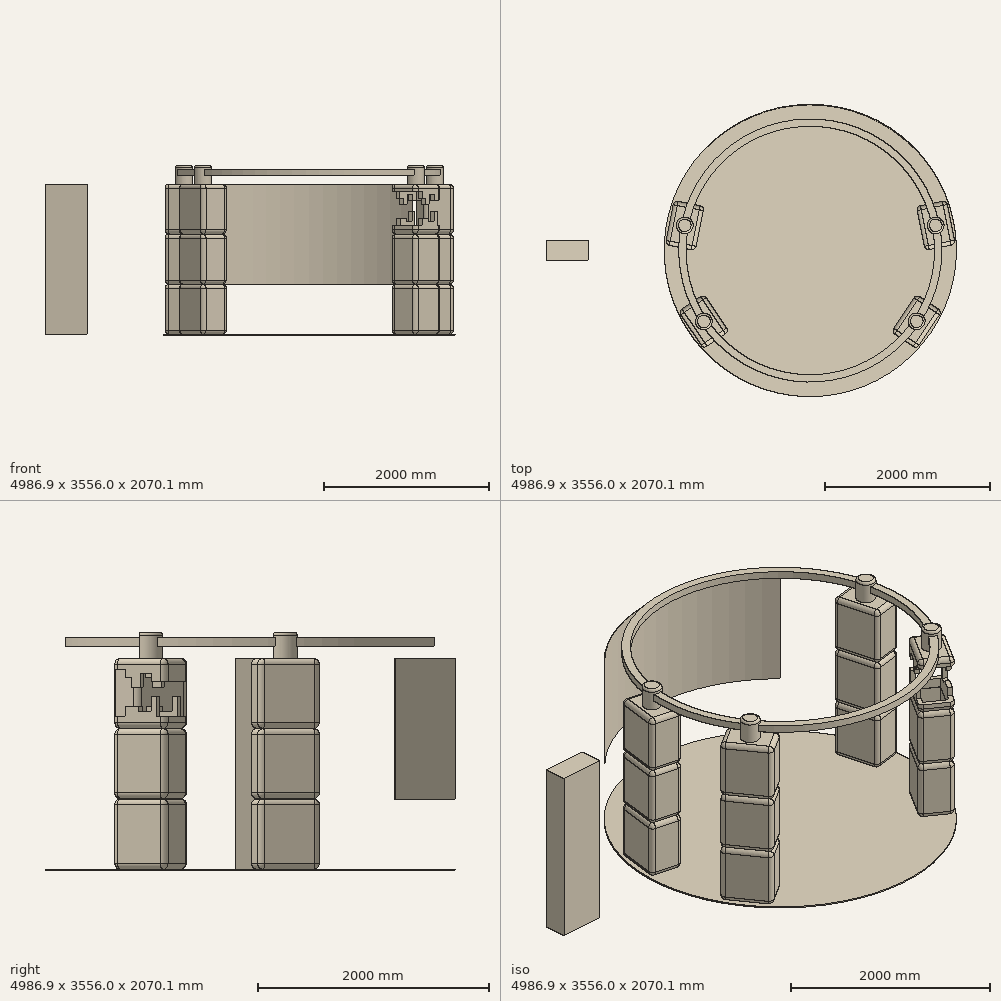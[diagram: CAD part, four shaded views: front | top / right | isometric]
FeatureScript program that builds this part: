
annotation { "Feature Type Name" : "Feature", "Feature Type Description" : "" }
export const myFeature = defineFeature(function(context is Context, id is Id, definition is map)
    precondition{}
    {
        {
            var Q0;
            Q0=qCreatedBy(makeId("Top.planeOp"),FACE);
            var sketch = newSketch(context, id + "F0", { "sketchPlane" : qUnion([Q0])});
            skCircle(sketch, "E0", {"center": v(0, 0) * mm, "radius": 1778 * mm});
            skSolve(sketch);
        }
        {
            var Q0;
            Q0 = qSketchRegion(id + "F0", true);
            extrude(context, id + "F1", {"entities" : qUnion([Q0]), "oppositeDirection" : true, "depth" : 12.7 * mm, "offsetDistance" : 25.4 * mm});
        }
        {
            var Q0;
            Q0=makeQuery(id+"F1.opExtrude","CAP_FACE",FACE,{"disambiguationData":[OSD([sQuery(id+"F0.wireOp",EDGE,"E0")])],"isStart":true});
            var sketch = newSketch(context, id + "F2", { "sketchPlane" : qUnion([Q0])});
            skLineSegment(sketch, "E1", {"start": v(0, -1778) * mm, "end": v(0, 1778) * mm});
            skLineSegment(sketch, "E2", {"start": v(-1778, 0) * mm, "end": v(1778, 0) * mm});
            skLineSegment(sketch, "E3.bottom", {"start": v(-1778, -1778) * mm, "end": v(1778, -1778) * mm});
            skLineSegment(sketch, "E3.top", {"start": v(-1778, 1778) * mm, "end": v(1778, 1778) * mm});
            skLineSegment(sketch, "E3.left", {"start": v(-1778, -1778) * mm, "end": v(-1778, 1778) * mm});
            skLineSegment(sketch, "E3.right", {"start": v(1778, -1778) * mm, "end": v(1778, 1778) * mm});
            skPoint(sketch, "E3.middle", {"position": v(0, 0) * mm});
            skLineSegment(sketch, "E4", {"start": v(-1778, -1778) * mm, "end": v(1778, 1778) * mm});
            skLineSegment(sketch, "E5", {"start": v(1778, -1778) * mm, "end": v(-1778, 1778) * mm});
            skCircle(sketch, "E6", {"center": v(0, 0) * mm, "radius": 1778 * mm});
            skCircle(sketch, "E7", {"center": v(0, 0) * mm, "radius": 1905 * mm});
            skLineSegment(sketch, "E8", {"start": v(0, -1422.31) * mm, "end": v(-1066.92, -1422.31) * mm});
            skLineSegment(sketch, "E9", {"start": v(0, -1422.31) * mm, "end": v(1066.92, -1422.31) * mm});
            skLineSegment(sketch, "E10", {"start": v(0, 0) * mm, "end": v(-1066.92, -1422.31) * mm});
            skLineSegment(sketch, "E11", {"start": v(0, 0) * mm, "end": v(1066.92, -1422.31) * mm});
            skLineSegment(sketch, "E12", {"start": v(0, 0) * mm, "end": v(-1143.12, -1523.9) * mm});
            skLineSegment(sketch, "E13", {"start": v(0, 0) * mm, "end": v(1143.12, -1523.9) * mm});
            skSolve(sketch);
        }
        {
            var Q0;
            Q0=makeQuery(id+"F1.opExtrude","CAP_FACE",FACE,{"disambiguationData":[OSD([sQuery(id+"F0.wireOp",EDGE,"E0")])],"isStart":true});
            var sketch = newSketch(context, id + "F3", { "sketchPlane" : qUnion([Q0])});
            skLineSegment(sketch, "E14.bottom", {"start": v(-1778, 1778) * mm, "end": v(1778, 1778) * mm});
            skLineSegment(sketch, "E14.top", {"start": v(-1778, -1778) * mm, "end": v(1778, -1778) * mm});
            skLineSegment(sketch, "E14.left", {"start": v(-1778, 1778) * mm, "end": v(-1778, -1778) * mm});
            skLineSegment(sketch, "E14.right", {"start": v(1778, 1778) * mm, "end": v(1778, -1778) * mm});
            skPoint(sketch, "E14.middle", {"position": v(0, 0) * mm});
            skLineSegment(sketch, "E15", {"start": v(1778, 1778) * mm, "end": v(-1778, -1778) * mm});
            skLineSegment(sketch, "E16", {"start": v(-1778, 1778) * mm, "end": v(1778, -1778) * mm});
            skLineSegment(sketch, "E17", {"start": v(1778, 0) * mm, "end": v(-1778, 0) * mm});
            skLineSegment(sketch, "E18", {"start": v(-1778, -1778) * mm, "end": v(-1778, -889) * mm});
            skLineSegment(sketch, "E19", {"start": v(-1778, -889) * mm, "end": v(1778, -889) * mm});
            skLineSegment(sketch, "E20", {"start": v(-1778, 1778) * mm, "end": v(-1778, 889) * mm});
            skLineSegment(sketch, "E21", {"start": v(-1517.62, -628.62) * mm, "end": v(1517.62, 628.62) * mm});
            skLineSegment(sketch, "E22", {"start": v(1517.62, -628.62) * mm, "end": v(-1517.62, 628.62) * mm});
            skLineSegment(sketch, "E23", {"start": v(1404.74, 581.86) * mm, "end": v(1642.66, 680.41) * mm});
            skLineSegment(sketch, "E24", {"start": v(-1394.59, -577.66) * mm, "end": v(-1642.66, -680.41) * mm});
            skLineSegment(sketch, "E25", {"start": v(-1411, 584.46) * mm, "end": v(-1642.66, 680.41) * mm});
            skLineSegment(sketch, "E26", {"start": v(1385, -573.69) * mm, "end": v(1642.66, -680.41) * mm});
            skLineSegment(sketch, "E27", {"start": v(-1290.66, 534.6) * mm, "end": v(-1397, 0) * mm});
            skLineSegment(sketch, "E28", {"start": v(-1642.66, 680.41) * mm, "end": v(-1778, 0) * mm});
            skLineSegment(sketch, "E29", {"start": v(-1290.66, 534.6) * mm, "end": v(-1657.16, 607.5) * mm});
            skLineSegment(sketch, "E30", {"start": v(-1397, 0) * mm, "end": v(-1763.5, 72.9) * mm});
            skLineSegment(sketch, "E31", {"start": v(-1290.66, -534.6) * mm, "end": v(-987.83, -987.83) * mm});
            skLineSegment(sketch, "E32", {"start": v(-1257.24, -1257.24) * mm, "end": v(-1642.66, -680.41) * mm});
            skLineSegment(sketch, "E33", {"start": v(-1290.66, -534.6) * mm, "end": v(-1601.36, -742.21) * mm});
            skLineSegment(sketch, "E34", {"start": v(-987.83, -987.83) * mm, "end": v(-1298.53, -1195.43) * mm});
            skLineSegment(sketch, "E35", {"start": v(1290.66, -534.6) * mm, "end": v(987.83, -987.83) * mm});
            skLineSegment(sketch, "E36", {"start": v(1642.66, -680.41) * mm, "end": v(1257.24, -1257.24) * mm});
            skLineSegment(sketch, "E37", {"start": v(987.83, -987.83) * mm, "end": v(1298.53, -1195.43) * mm});
            skLineSegment(sketch, "E38", {"start": v(1290.66, -534.6) * mm, "end": v(1601.36, -742.21) * mm});
            skLineSegment(sketch, "E39", {"start": v(1642.66, 680.41) * mm, "end": v(1778, 0) * mm});
            skLineSegment(sketch, "E40", {"start": v(1290.66, 534.6) * mm, "end": v(1397, 0) * mm});
            skLineSegment(sketch, "E41", {"start": v(1397, 0) * mm, "end": v(1763.5, 72.9) * mm});
            skLineSegment(sketch, "E42", {"start": v(1290.66, 534.6) * mm, "end": v(1657.16, 607.5) * mm});
            skSolve(sketch);
        }
        {
            var Q0;
            Q0=qCreatedBy(makeId("Top.planeOp"),FACE);
            var sketch = newSketch(context, id + "F4", { "sketchPlane" : qUnion([Q0])});
            skLineSegment(sketch, "E43.bottom", {"start": v(-2700.9, -127) * mm, "end": v(-3208.9, -127) * mm});
            skLineSegment(sketch, "E43.top", {"start": v(-2700.9, 127) * mm, "end": v(-3208.9, 127) * mm});
            skLineSegment(sketch, "E43.left", {"start": v(-2700.9, -127) * mm, "end": v(-2700.9, 127) * mm});
            skLineSegment(sketch, "E43.right", {"start": v(-3208.9, -127) * mm, "end": v(-3208.9, 127) * mm});
            skPoint(sketch, "E43.middle", {"position": v(-2954.9, 0) * mm});
            skSolve(sketch);
        }
        {
            var Q0;
            Q0=makeQuery(id+"F4.imprint","IMPRINT",FACE,{"disambiguationData":[TD([[makeQuery(id+"F4.imprint","IMPRINT",EDGE,{"derivedFrom":sQuery(id+"F4.wireOp",EDGE,"E43.bottom")}),-1.0]])]});
            extrude(context, id + "F5", {"entities" : qUnion([Q0]), "depth" : 1828.8 * mm, "offsetDistance" : 25.4 * mm});
        }
        {
            var Q0;
            Q0=makeQuery(id+"F3.imprint","IMPRINT",FACE,{"disambiguationData":[TD([[makeQuery(id+"F3.imprint","IMPRINT",EDGE,{"derivedFrom":sQuery(id+"F3.wireOp",EDGE,"E27")}),-1.0]])]});
            var Q1;
            Q1=makeQuery(id+"F3.imprint","IMPRINT",FACE,{"disambiguationData":[TD([[makeQuery(id+"F3.imprint","IMPRINT",EDGE,{"derivedFrom":sQuery(id+"F3.wireOp",EDGE,"E40")}),1.0]])]});
            var Q2;
            {var subQ5=sQuery(id+"F3.wireOp",EDGE,"E33");Q2=makeQuery(id+"F3.imprint","IMPRINT",FACE,{"disambiguationData":[TD([[makeQuery(id+"F3.imprint","IMPRINT",EDGE,{"derivedFrom":subQ5}),1.0]])]});}
            var Q3;
            {var subQ5=sQuery(id+"F3.wireOp",EDGE,"E34");Q3=makeQuery(id+"F3.imprint","IMPRINT",FACE,{"disambiguationData":[TD([[makeQuery(id+"F3.imprint","IMPRINT",EDGE,{"derivedFrom":subQ5}),-1.0]])]});}
            var Q4;
            {var subQ5=sQuery(id+"F3.wireOp",EDGE,"E38");Q4=makeQuery(id+"F3.imprint","IMPRINT",FACE,{"disambiguationData":[TD([[makeQuery(id+"F3.imprint","IMPRINT",EDGE,{"derivedFrom":subQ5}),-1.0]])]});}
            var Q5;
            {var subQ5=sQuery(id+"F3.wireOp",EDGE,"E37");Q5=makeQuery(id+"F3.imprint","IMPRINT",FACE,{"disambiguationData":[TD([[makeQuery(id+"F3.imprint","IMPRINT",EDGE,{"derivedFrom":subQ5}),1.0]])]});}
            extrude(context, id + "F6", {"entities" : qUnion([Q0, Q1, Q2, Q3, Q4, Q5]), "depth" : 1828.8 * mm, "offsetDistance" : 25.4 * mm});
        }
        {
            var Q0;
            Q0=qCreatedBy(makeId("Front.planeOp"),FACE);
            var sketch = newSketch(context, id + "F7", { "sketchPlane" : qUnion([Q0])});
            skLineSegment(sketch, "E44", {"start": v(-207.03, 0) * mm, "end": v(-207.03, 609.6) * mm});
            skLineSegment(sketch, "E45", {"start": v(-207.03, 609.6) * mm, "end": v(-207.03, 1219.2) * mm});
            skLineSegment(sketch, "E46", {"start": v(-207.03, 1219.2) * mm, "end": v(-207.03, 1828.8) * mm});
            skLineSegment(sketch, "E47.bottom", {"start": v(-1849.74, 609.6) * mm, "end": v(1833.26, 609.6) * mm});
            skLineSegment(sketch, "E47.top", {"start": v(-1849.74, 612.14) * mm, "end": v(1833.26, 612.14) * mm});
            skLineSegment(sketch, "E47.left", {"start": v(-1849.74, 609.6) * mm, "end": v(-1849.74, 612.14) * mm});
            skLineSegment(sketch, "E47.right", {"start": v(1833.26, 609.6) * mm, "end": v(1833.26, 612.14) * mm});
            skLineSegment(sketch, "E48.bottom", {"start": v(-1849.74, 1219.2) * mm, "end": v(1833.26, 1219.2) * mm});
            skLineSegment(sketch, "E48.top", {"start": v(-1849.74, 1221.74) * mm, "end": v(1833.26, 1221.74) * mm});
            skLineSegment(sketch, "E48.left", {"start": v(-1849.74, 1219.2) * mm, "end": v(-1849.74, 1221.74) * mm});
            skLineSegment(sketch, "E48.right", {"start": v(1833.26, 1219.2) * mm, "end": v(1833.26, 1221.74) * mm});
            skSolve(sketch);
        }
        {
            var Q0;
            Q0 = qSketchRegion(id + "F7", true);
            extrude(context, id + "F8", {"entities" : qUnion([Q0]), "operationType" : NewBodyOperationType.REMOVE, "oppositeDirection" : true, "depth" : 1447.8 * mm, "offsetDistance" : 25.4 * mm, "hasSecondDirection" : true, "secondDirectionOppositeDirection" : false, "secondDirectionDepth" : 1905 * mm});
        }
        {
            var Q0;
            Q0=makeQuery(id+"F6.opExtrude","CAP_FACE",FACE,{"disambiguationData":[OSD([sQuery(id+"F3.wireOp",EDGE,"E39"),sQuery(id+"F3.wireOp",EDGE,"E40"),sQuery(id+"F3.wireOp",EDGE,"E41"),sQuery(id+"F3.wireOp",EDGE,"E42")])],"isStart":false});
            var Q1;
            {var subQ1=sQuery(id+"F3.wireOp",EDGE,"E42");Q1=makeQuery(id+"F8.boolean.opBoolean","SPLIT",FACE,{"disambiguationData":[TD([makeQuery(id+"F8.opExtrude","SWEPT_FACE",FACE,{"disambiguationData":[OSD([sQuery(id+"F7.wireOp",EDGE,"E48.top")])]})])],"derivedFrom":makeQuery(id+"F6.opExtrude","SWEPT_FACE",FACE,{"disambiguationData":[OSD([subQ1])]})});}
            var Q2;
            {var subQ2=sQuery(id+"F3.wireOp",EDGE,"E40");Q2=makeQuery(id+"F8.boolean.opBoolean","SPLIT",FACE,{"disambiguationData":[TD([makeQuery(id+"F8.opExtrude","SWEPT_FACE",FACE,{"disambiguationData":[OSD([sQuery(id+"F7.wireOp",EDGE,"E48.top")])]})])],"derivedFrom":makeQuery(id+"F6.opExtrude","SWEPT_FACE",FACE,{"disambiguationData":[OSD([subQ2])]})});}
            var Q3;
            {var subQ1=sQuery(id+"F3.wireOp",EDGE,"E41");Q3=makeQuery(id+"F8.boolean.opBoolean","SPLIT",FACE,{"disambiguationData":[TD([makeQuery(id+"F8.opExtrude","SWEPT_FACE",FACE,{"disambiguationData":[OSD([sQuery(id+"F7.wireOp",EDGE,"E48.top")])]})])],"derivedFrom":makeQuery(id+"F6.opExtrude","SWEPT_FACE",FACE,{"disambiguationData":[OSD([subQ1])]})});}
            var Q4;
            {var subQ2=sQuery(id+"F3.wireOp",EDGE,"E39");Q4=makeQuery(id+"F8.boolean.opBoolean","SPLIT",FACE,{"disambiguationData":[TD([makeQuery(id+"F8.opExtrude","SWEPT_FACE",FACE,{"disambiguationData":[OSD([sQuery(id+"F7.wireOp",EDGE,"E48.top")])]})])],"derivedFrom":makeQuery(id+"F6.opExtrude","SWEPT_FACE",FACE,{"disambiguationData":[OSD([subQ2])]})});}
            var Q5;
            Q5=makeQuery(id+"F8.boolean.opBoolean","SPLIT",FACE,{"disambiguationData":[TD([makeQuery(id+"F8.opExtrude","SWEPT_FACE",FACE,{"disambiguationData":[OSD([sQuery(id+"F7.wireOp",EDGE,"E47.top")])]})])],"derivedFrom":makeQuery(id+"F6.opExtrude","SWEPT_FACE",FACE,{"disambiguationData":[OSD([sQuery(id+"F3.wireOp",EDGE,"E39")])]})});
            var Q6;
            Q6=makeQuery(id+"F8.boolean.opBoolean","SPLIT",FACE,{"disambiguationData":[TD([makeQuery(id+"F8.opExtrude","SWEPT_FACE",FACE,{"disambiguationData":[OSD([sQuery(id+"F7.wireOp",EDGE,"E47.top")])]})])],"derivedFrom":makeQuery(id+"F6.opExtrude","SWEPT_FACE",FACE,{"disambiguationData":[OSD([sQuery(id+"F3.wireOp",EDGE,"E40")])]})});
            var Q7;
            Q7=makeQuery(id+"F8.boolean.opBoolean","SPLIT",FACE,{"disambiguationData":[TD([makeQuery(id+"F8.opExtrude","SWEPT_FACE",FACE,{"disambiguationData":[OSD([sQuery(id+"F7.wireOp",EDGE,"E47.top")])]})])],"derivedFrom":makeQuery(id+"F6.opExtrude","SWEPT_FACE",FACE,{"disambiguationData":[OSD([sQuery(id+"F3.wireOp",EDGE,"E41")])]})});
            var Q8;
            Q8=makeQuery(id+"F8.boolean.opBoolean","SPLIT",FACE,{"disambiguationData":[TD([makeQuery(id+"F8.opExtrude","SWEPT_FACE",FACE,{"disambiguationData":[OSD([sQuery(id+"F7.wireOp",EDGE,"E47.top")])]})])],"derivedFrom":makeQuery(id+"F6.opExtrude","SWEPT_FACE",FACE,{"disambiguationData":[OSD([sQuery(id+"F3.wireOp",EDGE,"E42")])]})});
            var Q9;
            Q9=makeQuery(id+"F8.boolean.opBoolean","SPLIT",FACE,{"disambiguationData":[TD([makeQuery(id+"F8.opExtrude","SWEPT_FACE",FACE,{"disambiguationData":[OSD([sQuery(id+"F7.wireOp",EDGE,"E47.top")])]})])],"derivedFrom":makeQuery(id+"F6.opExtrude","SWEPT_FACE",FACE,{"disambiguationData":[OSD([sQuery(id+"F3.wireOp",EDGE,"E36")])]})});
            var Q10;
            {var subQ2=sQuery(id+"F3.wireOp",EDGE,"E36");Q10=makeQuery(id+"F8.boolean.opBoolean","SPLIT",FACE,{"disambiguationData":[TD([makeQuery(id+"F8.opExtrude","SWEPT_FACE",FACE,{"disambiguationData":[OSD([sQuery(id+"F7.wireOp",EDGE,"E48.top")])]})])],"derivedFrom":makeQuery(id+"F6.opExtrude","SWEPT_FACE",FACE,{"disambiguationData":[OSD([subQ2])]})});}
            var Q11;
            Q11=makeQuery(id+"F6.opExtrude","CAP_FACE",FACE,{"disambiguationData":[OSD([sQuery(id+"F3.wireOp",EDGE,"E35"),sQuery(id+"F3.wireOp",EDGE,"E36"),sQuery(id+"F3.wireOp",EDGE,"E37"),sQuery(id+"F3.wireOp",EDGE,"E38")])],"isStart":false});
            var Q12;
            {var subQ1=sQuery(id+"F3.wireOp",EDGE,"E38");Q12=makeQuery(id+"F8.boolean.opBoolean","SPLIT",FACE,{"disambiguationData":[TD([makeQuery(id+"F8.opExtrude","SWEPT_FACE",FACE,{"disambiguationData":[OSD([sQuery(id+"F7.wireOp",EDGE,"E48.top")])]})])],"derivedFrom":makeQuery(id+"F6.opExtrude","SWEPT_FACE",FACE,{"disambiguationData":[OSD([subQ1])]})});}
            var Q13;
            {var subQ0=sQuery(id+"F3.wireOp",EDGE,"E35");var subQ1=sQuery(id+"F3.wireOp",EDGE,"E38");Q13=makeQuery(id+"F8.boolean.opBoolean","SPLIT",EDGE,{"disambiguationData":[TD([makeQuery(id+"F8.opExtrude","SWEPT_FACE",FACE,{"disambiguationData":[OSD([sQuery(id+"F7.wireOp",EDGE,"E47.top")])]})])],"derivedFrom":makeQuery(id+"F6.opExtrude","SWEPT_EDGE",EDGE,{"disambiguationData":[OSD([sQuery(id+"F3.wireOp",EDGE,"E22"),subQ0,subQ1])]})});}
            var Q14;
            {var subQ2=sQuery(id+"F3.wireOp",EDGE,"E35");Q14=makeQuery(id+"F8.boolean.opBoolean","SPLIT",FACE,{"disambiguationData":[TD([makeQuery(id+"F8.opExtrude","SWEPT_FACE",FACE,{"disambiguationData":[OSD([sQuery(id+"F7.wireOp",EDGE,"E48.top")])]})])],"derivedFrom":makeQuery(id+"F6.opExtrude","SWEPT_FACE",FACE,{"disambiguationData":[OSD([subQ2])]})});}
            var Q15;
            Q15=makeQuery(id+"F8.boolean.opBoolean","SPLIT",FACE,{"disambiguationData":[TD([makeQuery(id+"F8.opExtrude","SWEPT_FACE",FACE,{"disambiguationData":[OSD([sQuery(id+"F7.wireOp",EDGE,"E47.top")])]})])],"derivedFrom":makeQuery(id+"F6.opExtrude","SWEPT_FACE",FACE,{"disambiguationData":[OSD([sQuery(id+"F3.wireOp",EDGE,"E35")])]})});
            var Q16;
            Q16=makeQuery(id+"F6.opExtrude","CAP_FACE",FACE,{"disambiguationData":[OSD([sQuery(id+"F3.wireOp",EDGE,"E27"),sQuery(id+"F3.wireOp",EDGE,"E28"),sQuery(id+"F3.wireOp",EDGE,"E29"),sQuery(id+"F3.wireOp",EDGE,"E30")])],"isStart":false});
            var Q17;
            {var subQ1=sQuery(id+"F3.wireOp",EDGE,"E29");Q17=makeQuery(id+"F8.boolean.opBoolean","SPLIT",FACE,{"disambiguationData":[TD([makeQuery(id+"F8.opExtrude","SWEPT_FACE",FACE,{"disambiguationData":[OSD([sQuery(id+"F7.wireOp",EDGE,"E48.top")])]})])],"derivedFrom":makeQuery(id+"F6.opExtrude","SWEPT_FACE",FACE,{"disambiguationData":[OSD([subQ1])]})});}
            var Q18;
            Q18=makeQuery(id+"F8.boolean.opBoolean","SPLIT",FACE,{"disambiguationData":[TD([makeQuery(id+"F8.opExtrude","SWEPT_FACE",FACE,{"disambiguationData":[OSD([sQuery(id+"F7.wireOp",EDGE,"E47.top")])]})])],"derivedFrom":makeQuery(id+"F6.opExtrude","SWEPT_FACE",FACE,{"disambiguationData":[OSD([sQuery(id+"F3.wireOp",EDGE,"E29")])]})});
            var Q19;
            Q19=makeQuery(id+"F8.boolean.opBoolean","SPLIT",FACE,{"disambiguationData":[TD([makeQuery(id+"F8.opExtrude","SWEPT_FACE",FACE,{"disambiguationData":[OSD([sQuery(id+"F7.wireOp",EDGE,"E47.top")])]})])],"derivedFrom":makeQuery(id+"F6.opExtrude","SWEPT_FACE",FACE,{"disambiguationData":[OSD([sQuery(id+"F3.wireOp",EDGE,"E28")])]})});
            var Q20;
            {var subQ2=sQuery(id+"F3.wireOp",EDGE,"E28");Q20=makeQuery(id+"F8.boolean.opBoolean","SPLIT",FACE,{"disambiguationData":[TD([makeQuery(id+"F8.opExtrude","SWEPT_FACE",FACE,{"disambiguationData":[OSD([sQuery(id+"F7.wireOp",EDGE,"E48.top")])]})])],"derivedFrom":makeQuery(id+"F6.opExtrude","SWEPT_FACE",FACE,{"disambiguationData":[OSD([subQ2])]})});}
            var Q21;
            Q21=makeQuery(id+"F8.boolean.opBoolean","SPLIT",FACE,{"disambiguationData":[TD([makeQuery(id+"F8.opExtrude","SWEPT_FACE",FACE,{"disambiguationData":[OSD([sQuery(id+"F7.wireOp",EDGE,"E47.top")])]})])],"derivedFrom":makeQuery(id+"F6.opExtrude","SWEPT_FACE",FACE,{"disambiguationData":[OSD([sQuery(id+"F3.wireOp",EDGE,"E33")])]})});
            var Q22;
            {var subQ1=sQuery(id+"F3.wireOp",EDGE,"E37");Q22=makeQuery(id+"F8.boolean.opBoolean","SPLIT",FACE,{"disambiguationData":[TD([makeQuery(id+"F8.opExtrude","SWEPT_FACE",FACE,{"disambiguationData":[OSD([sQuery(id+"F7.wireOp",EDGE,"E48.top")])]})])],"derivedFrom":makeQuery(id+"F6.opExtrude","SWEPT_FACE",FACE,{"disambiguationData":[OSD([subQ1])]})});}
            var Q23;
            Q23=makeQuery(id+"F8.boolean.opBoolean","SPLIT",FACE,{"disambiguationData":[TD([makeQuery(id+"F8.opExtrude","SWEPT_FACE",FACE,{"disambiguationData":[OSD([sQuery(id+"F7.wireOp",EDGE,"E47.top")])]})])],"derivedFrom":makeQuery(id+"F6.opExtrude","SWEPT_FACE",FACE,{"disambiguationData":[OSD([sQuery(id+"F3.wireOp",EDGE,"E37")])]})});
            var Q24;
            {var subQ2=sQuery(id+"F3.wireOp",EDGE,"E32");Q24=makeQuery(id+"F8.boolean.opBoolean","SPLIT",FACE,{"disambiguationData":[TD([makeQuery(id+"F8.opExtrude","SWEPT_FACE",FACE,{"disambiguationData":[OSD([sQuery(id+"F7.wireOp",EDGE,"E48.top")])]})])],"derivedFrom":makeQuery(id+"F6.opExtrude","SWEPT_FACE",FACE,{"disambiguationData":[OSD([subQ2])]})});}
            var Q25;
            Q25=makeQuery(id+"F8.boolean.opBoolean","SPLIT",FACE,{"disambiguationData":[TD([makeQuery(id+"F8.opExtrude","SWEPT_FACE",FACE,{"disambiguationData":[OSD([sQuery(id+"F7.wireOp",EDGE,"E47.top")])]})])],"derivedFrom":makeQuery(id+"F6.opExtrude","SWEPT_FACE",FACE,{"disambiguationData":[OSD([sQuery(id+"F3.wireOp",EDGE,"E32")])]})});
            var Q26;
            {var subQ1=sQuery(id+"F3.wireOp",EDGE,"E30");Q26=makeQuery(id+"F8.boolean.opBoolean","SPLIT",FACE,{"disambiguationData":[TD([makeQuery(id+"F8.opExtrude","SWEPT_FACE",FACE,{"disambiguationData":[OSD([sQuery(id+"F7.wireOp",EDGE,"E48.top")])]})])],"derivedFrom":makeQuery(id+"F6.opExtrude","SWEPT_FACE",FACE,{"disambiguationData":[OSD([subQ1])]})});}
            var Q27;
            Q27=makeQuery(id+"F8.boolean.opBoolean","SPLIT",FACE,{"disambiguationData":[TD([makeQuery(id+"F8.opExtrude","SWEPT_FACE",FACE,{"disambiguationData":[OSD([sQuery(id+"F7.wireOp",EDGE,"E47.top")])]})])],"derivedFrom":makeQuery(id+"F6.opExtrude","SWEPT_FACE",FACE,{"disambiguationData":[OSD([sQuery(id+"F3.wireOp",EDGE,"E30")])]})});
            var Q28;
            Q28=makeQuery(id+"F6.opExtrude","CAP_FACE",FACE,{"disambiguationData":[OSD([sQuery(id+"F3.wireOp",EDGE,"E31"),sQuery(id+"F3.wireOp",EDGE,"E32"),sQuery(id+"F3.wireOp",EDGE,"E33"),sQuery(id+"F3.wireOp",EDGE,"E34")])],"isStart":false});
            var Q29;
            {var subQ1=sQuery(id+"F3.wireOp",EDGE,"E33");Q29=makeQuery(id+"F8.boolean.opBoolean","SPLIT",FACE,{"disambiguationData":[TD([makeQuery(id+"F8.opExtrude","SWEPT_FACE",FACE,{"disambiguationData":[OSD([sQuery(id+"F7.wireOp",EDGE,"E48.top")])]})])],"derivedFrom":makeQuery(id+"F6.opExtrude","SWEPT_FACE",FACE,{"disambiguationData":[OSD([subQ1])]})});}
            var Q30;
            Q30=makeQuery(id+"F8.boolean.opBoolean","SPLIT",FACE,{"disambiguationData":[TD([makeQuery(id+"F8.opExtrude","SWEPT_FACE",FACE,{"disambiguationData":[OSD([sQuery(id+"F7.wireOp",EDGE,"E47.top")])]})])],"derivedFrom":makeQuery(id+"F6.opExtrude","SWEPT_FACE",FACE,{"disambiguationData":[OSD([sQuery(id+"F3.wireOp",EDGE,"E27")])]})});
            var Q31;
            {var subQ2=sQuery(id+"F3.wireOp",EDGE,"E27");Q31=makeQuery(id+"F8.boolean.opBoolean","SPLIT",FACE,{"disambiguationData":[TD([makeQuery(id+"F8.opExtrude","SWEPT_FACE",FACE,{"disambiguationData":[OSD([sQuery(id+"F7.wireOp",EDGE,"E48.top")])]})])],"derivedFrom":makeQuery(id+"F6.opExtrude","SWEPT_FACE",FACE,{"disambiguationData":[OSD([subQ2])]})});}
            var Q32;
            Q32=makeQuery(id+"F8.boolean.opBoolean","SPLIT",FACE,{"disambiguationData":[TD([makeQuery(id+"F8.opExtrude","SWEPT_FACE",FACE,{"disambiguationData":[OSD([sQuery(id+"F7.wireOp",EDGE,"E47.top")])]})])],"derivedFrom":makeQuery(id+"F6.opExtrude","SWEPT_FACE",FACE,{"disambiguationData":[OSD([sQuery(id+"F3.wireOp",EDGE,"E34")])]})});
            var Q33;
            {var subQ1=sQuery(id+"F3.wireOp",EDGE,"E34");Q33=makeQuery(id+"F8.boolean.opBoolean","SPLIT",FACE,{"disambiguationData":[TD([makeQuery(id+"F8.opExtrude","SWEPT_FACE",FACE,{"disambiguationData":[OSD([sQuery(id+"F7.wireOp",EDGE,"E48.top")])]})])],"derivedFrom":makeQuery(id+"F6.opExtrude","SWEPT_FACE",FACE,{"disambiguationData":[OSD([subQ1])]})});}
            var Q34;
            Q34=makeQuery(id+"F8.boolean.opBoolean","SPLIT",FACE,{"disambiguationData":[TD([makeQuery(id+"F8.opExtrude","SWEPT_FACE",FACE,{"disambiguationData":[OSD([sQuery(id+"F7.wireOp",EDGE,"E47.top")])]})])],"derivedFrom":makeQuery(id+"F6.opExtrude","SWEPT_FACE",FACE,{"disambiguationData":[OSD([sQuery(id+"F3.wireOp",EDGE,"E31")])]})});
            var Q35;
            {var subQ2=sQuery(id+"F3.wireOp",EDGE,"E31");Q35=makeQuery(id+"F8.boolean.opBoolean","SPLIT",FACE,{"disambiguationData":[TD([makeQuery(id+"F8.opExtrude","SWEPT_FACE",FACE,{"disambiguationData":[OSD([sQuery(id+"F7.wireOp",EDGE,"E48.top")])]})])],"derivedFrom":makeQuery(id+"F6.opExtrude","SWEPT_FACE",FACE,{"disambiguationData":[OSD([subQ2])]})});}
            var Q36;
            Q36=makeQuery(id+"F8.boolean.opBoolean","SPLIT",FACE,{"disambiguationData":[TD([makeQuery(id+"F8.opExtrude","SWEPT_FACE",FACE,{"disambiguationData":[OSD([sQuery(id+"F7.wireOp",EDGE,"E47.top")])]})])],"derivedFrom":makeQuery(id+"F6.opExtrude","SWEPT_FACE",FACE,{"disambiguationData":[OSD([sQuery(id+"F3.wireOp",EDGE,"E38")])]})});
            fillet(context, id + "F9", {"entities" : qUnion([Q0, Q1, Q2, Q3, Q4, Q5, Q6, Q7, Q8, Q9, Q10, Q11, Q12, Q13, Q14, Q15, Q16, Q17, Q18, Q19, Q20, Q21, Q22, Q23, Q24, Q25, Q26, Q27, Q28, Q29, Q30, Q31, Q32, Q33, Q34, Q35, Q36]), "radius" : 50.8 * mm, "tangentPropagation" : true, "allowEdgeOverflow" : false});
        }
        {
            var Q0;
            {var subQ2=sQuery(id+"F3.wireOp",EDGE,"E28");Q0=makeQuery(id+"F8.boolean.opBoolean","SPLIT",FACE,{"disambiguationData":[TD([makeQuery(id+"F8.opExtrude","SWEPT_FACE",FACE,{"disambiguationData":[OSD([sQuery(id+"F7.wireOp",EDGE,"E47.bottom")])]})])],"derivedFrom":makeQuery(id+"F6.opExtrude","SWEPT_FACE",FACE,{"disambiguationData":[OSD([subQ2])]})});}
            var Q1;
            {var subQ1=sQuery(id+"F3.wireOp",EDGE,"E29");Q1=makeQuery(id+"F8.boolean.opBoolean","SPLIT",FACE,{"disambiguationData":[TD([makeQuery(id+"F8.opExtrude","SWEPT_FACE",FACE,{"disambiguationData":[OSD([sQuery(id+"F7.wireOp",EDGE,"E47.bottom")])]})])],"derivedFrom":makeQuery(id+"F6.opExtrude","SWEPT_FACE",FACE,{"disambiguationData":[OSD([subQ1])]})});}
            var Q2;
            {var subQ1=sQuery(id+"F3.wireOp",EDGE,"E30");Q2=makeQuery(id+"F8.boolean.opBoolean","SPLIT",FACE,{"disambiguationData":[TD([makeQuery(id+"F8.opExtrude","SWEPT_FACE",FACE,{"disambiguationData":[OSD([sQuery(id+"F7.wireOp",EDGE,"E47.bottom")])]})])],"derivedFrom":makeQuery(id+"F6.opExtrude","SWEPT_FACE",FACE,{"disambiguationData":[OSD([subQ1])]})});}
            var Q3;
            {var subQ2=sQuery(id+"F3.wireOp",EDGE,"E27");Q3=makeQuery(id+"F8.boolean.opBoolean","SPLIT",FACE,{"disambiguationData":[TD([makeQuery(id+"F8.opExtrude","SWEPT_FACE",FACE,{"disambiguationData":[OSD([sQuery(id+"F7.wireOp",EDGE,"E47.bottom")])]})])],"derivedFrom":makeQuery(id+"F6.opExtrude","SWEPT_FACE",FACE,{"disambiguationData":[OSD([subQ2])]})});}
            var Q4;
            {var subQ1=sQuery(id+"F3.wireOp",EDGE,"E34");Q4=makeQuery(id+"F8.boolean.opBoolean","SPLIT",FACE,{"disambiguationData":[TD([makeQuery(id+"F8.opExtrude","SWEPT_FACE",FACE,{"disambiguationData":[OSD([sQuery(id+"F7.wireOp",EDGE,"E47.bottom")])]})])],"derivedFrom":makeQuery(id+"F6.opExtrude","SWEPT_FACE",FACE,{"disambiguationData":[OSD([subQ1])]})});}
            var Q5;
            {var subQ2=sQuery(id+"F3.wireOp",EDGE,"E31");Q5=makeQuery(id+"F8.boolean.opBoolean","SPLIT",FACE,{"disambiguationData":[TD([makeQuery(id+"F8.opExtrude","SWEPT_FACE",FACE,{"disambiguationData":[OSD([sQuery(id+"F7.wireOp",EDGE,"E47.bottom")])]})])],"derivedFrom":makeQuery(id+"F6.opExtrude","SWEPT_FACE",FACE,{"disambiguationData":[OSD([subQ2])]})});}
            var Q6;
            {var subQ2=sQuery(id+"F3.wireOp",EDGE,"E32");Q6=makeQuery(id+"F8.boolean.opBoolean","SPLIT",FACE,{"disambiguationData":[TD([makeQuery(id+"F8.opExtrude","SWEPT_FACE",FACE,{"disambiguationData":[OSD([sQuery(id+"F7.wireOp",EDGE,"E47.bottom")])]})])],"derivedFrom":makeQuery(id+"F6.opExtrude","SWEPT_FACE",FACE,{"disambiguationData":[OSD([subQ2])]})});}
            var Q7;
            {var subQ1=sQuery(id+"F3.wireOp",EDGE,"E33");Q7=makeQuery(id+"F8.boolean.opBoolean","SPLIT",FACE,{"disambiguationData":[TD([makeQuery(id+"F8.opExtrude","SWEPT_FACE",FACE,{"disambiguationData":[OSD([sQuery(id+"F7.wireOp",EDGE,"E47.bottom")])]})])],"derivedFrom":makeQuery(id+"F6.opExtrude","SWEPT_FACE",FACE,{"disambiguationData":[OSD([subQ1])]})});}
            var Q8;
            {var subQ2=sQuery(id+"F3.wireOp",EDGE,"E35");Q8=makeQuery(id+"F8.boolean.opBoolean","SPLIT",FACE,{"disambiguationData":[TD([makeQuery(id+"F8.opExtrude","SWEPT_FACE",FACE,{"disambiguationData":[OSD([sQuery(id+"F7.wireOp",EDGE,"E47.bottom")])]})])],"derivedFrom":makeQuery(id+"F6.opExtrude","SWEPT_FACE",FACE,{"disambiguationData":[OSD([subQ2])]})});}
            var Q9;
            {var subQ2=sQuery(id+"F3.wireOp",EDGE,"E40");Q9=makeQuery(id+"F8.boolean.opBoolean","SPLIT",FACE,{"disambiguationData":[TD([makeQuery(id+"F8.opExtrude","SWEPT_FACE",FACE,{"disambiguationData":[OSD([sQuery(id+"F7.wireOp",EDGE,"E47.bottom")])]})])],"derivedFrom":makeQuery(id+"F6.opExtrude","SWEPT_FACE",FACE,{"disambiguationData":[OSD([subQ2])]})});}
            var Q10;
            {var subQ1=sQuery(id+"F3.wireOp",EDGE,"E42");Q10=makeQuery(id+"F8.boolean.opBoolean","SPLIT",FACE,{"disambiguationData":[TD([makeQuery(id+"F8.opExtrude","SWEPT_FACE",FACE,{"disambiguationData":[OSD([sQuery(id+"F7.wireOp",EDGE,"E47.bottom")])]})])],"derivedFrom":makeQuery(id+"F6.opExtrude","SWEPT_FACE",FACE,{"disambiguationData":[OSD([subQ1])]})});}
            var Q11;
            {var subQ1=sQuery(id+"F3.wireOp",EDGE,"E41");Q11=makeQuery(id+"F8.boolean.opBoolean","SPLIT",FACE,{"disambiguationData":[TD([makeQuery(id+"F8.opExtrude","SWEPT_FACE",FACE,{"disambiguationData":[OSD([sQuery(id+"F7.wireOp",EDGE,"E47.bottom")])]})])],"derivedFrom":makeQuery(id+"F6.opExtrude","SWEPT_FACE",FACE,{"disambiguationData":[OSD([subQ1])]})});}
            var Q12;
            {var subQ1=sQuery(id+"F3.wireOp",EDGE,"E37");Q12=makeQuery(id+"F8.boolean.opBoolean","SPLIT",FACE,{"disambiguationData":[TD([makeQuery(id+"F8.opExtrude","SWEPT_FACE",FACE,{"disambiguationData":[OSD([sQuery(id+"F7.wireOp",EDGE,"E47.bottom")])]})])],"derivedFrom":makeQuery(id+"F6.opExtrude","SWEPT_FACE",FACE,{"disambiguationData":[OSD([subQ1])]})});}
            var Q13;
            {var subQ2=sQuery(id+"F3.wireOp",EDGE,"E36");Q13=makeQuery(id+"F8.boolean.opBoolean","SPLIT",FACE,{"disambiguationData":[TD([makeQuery(id+"F8.opExtrude","SWEPT_FACE",FACE,{"disambiguationData":[OSD([sQuery(id+"F7.wireOp",EDGE,"E47.bottom")])]})])],"derivedFrom":makeQuery(id+"F6.opExtrude","SWEPT_FACE",FACE,{"disambiguationData":[OSD([subQ2])]})});}
            var Q14;
            {var subQ2=sQuery(id+"F3.wireOp",EDGE,"E39");Q14=makeQuery(id+"F8.boolean.opBoolean","SPLIT",FACE,{"disambiguationData":[TD([makeQuery(id+"F8.opExtrude","SWEPT_FACE",FACE,{"disambiguationData":[OSD([sQuery(id+"F7.wireOp",EDGE,"E47.bottom")])]})])],"derivedFrom":makeQuery(id+"F6.opExtrude","SWEPT_FACE",FACE,{"disambiguationData":[OSD([subQ2])]})});}
            var Q15;
            {var subQ1=sQuery(id+"F3.wireOp",EDGE,"E38");Q15=makeQuery(id+"F8.boolean.opBoolean","SPLIT",FACE,{"disambiguationData":[TD([makeQuery(id+"F8.opExtrude","SWEPT_FACE",FACE,{"disambiguationData":[OSD([sQuery(id+"F7.wireOp",EDGE,"E47.bottom")])]})])],"derivedFrom":makeQuery(id+"F6.opExtrude","SWEPT_FACE",FACE,{"disambiguationData":[OSD([subQ1])]})});}
            fillet(context, id + "F10", {"entities" : qUnion([Q0, Q1, Q2, Q3, Q4, Q5, Q6, Q7, Q8, Q9, Q10, Q11, Q12, Q13, Q14, Q15]), "radius" : 50.8 * mm, "tangentPropagation" : true, "allowEdgeOverflow" : false});
        }
        {
            var Q0;
            Q0=makeQuery(id+"F1.opExtrude","CAP_FACE",FACE,{"disambiguationData":[OSD([sQuery(id+"F0.wireOp",EDGE,"E0")])],"isStart":true});
            cPlane(context, id + "F11", {"entities" : qUnion([Q0]), "cplaneType" : CPlaneType.OFFSET, "offset" : 1828.8 * mm, "width" : 152.4 * mm, "height" : 152.4 * mm});
        }
        {
            var Q0;
            Q0=qCreatedBy(id+"F11.planeOp",FACE);
            var sketch = newSketch(context, id + "F12", { "sketchPlane" : qUnion([Q0])});
            skCircle(sketch, "E49", {"center": v(0, 0) * mm, "radius": 1555.75 * mm});
            skCircle(sketch, "E50", {"center": v(-1525.84, 303.62) * mm, "radius": 101.6 * mm});
            skCircle(sketch, "E51", {"center": v(-1293.5, -864.4) * mm, "radius": 101.6 * mm});
            skCircle(sketch, "E52", {"center": v(1294.87, -862.36) * mm, "radius": 101.6 * mm});
            skCircle(sketch, "E53", {"center": v(1525.85, 303.56) * mm, "radius": 101.6 * mm});
            skSolve(sketch);
        }
        {
            var Q0;
            {var subQ0=sQuery(id+"F12.wireOp",EDGE,"E50");var subQ1=sQuery(id+"F12.wireOp",EDGE,"E49");var subQ2=makeQuery(id+"F12.imprint","INTERSECT",VERTEX,{"disambiguationData":[OD(0.0)],"derivedFrom":[subQ1,subQ0]});Q0=makeQuery(id+"F12.imprint","IMPRINT",FACE,{"disambiguationData":[TD([[makeQuery(id+"F12.imprint","IMPRINT",EDGE,{"disambiguationData":[TD([[subQ2,-1.0]])],"derivedFrom":subQ1}),1.0]])]});}
            var Q1;
            {var subQ0=sQuery(id+"F12.wireOp",EDGE,"E50");var subQ1=sQuery(id+"F12.wireOp",EDGE,"E49");var subQ2=makeQuery(id+"F12.imprint","INTERSECT",VERTEX,{"disambiguationData":[OD(0.0)],"derivedFrom":[subQ1,subQ0]});Q1=makeQuery(id+"F12.imprint","IMPRINT",FACE,{"disambiguationData":[TD([[makeQuery(id+"F12.imprint","IMPRINT",EDGE,{"disambiguationData":[TD([[subQ2,-1.0]])],"derivedFrom":subQ1}),-1.0]])]});}
            var Q2;
            {var subQ0=sQuery(id+"F12.wireOp",EDGE,"E51");var subQ1=sQuery(id+"F12.wireOp",EDGE,"E49");var subQ2=makeQuery(id+"F12.imprint","INTERSECT",VERTEX,{"disambiguationData":[OD(0.0)],"derivedFrom":[subQ1,subQ0]});Q2=makeQuery(id+"F12.imprint","IMPRINT",FACE,{"disambiguationData":[TD([[makeQuery(id+"F12.imprint","IMPRINT",EDGE,{"disambiguationData":[TD([[subQ2,-1.0]])],"derivedFrom":subQ1}),-1.0]])]});}
            var Q3;
            {var subQ0=sQuery(id+"F12.wireOp",EDGE,"E51");var subQ1=sQuery(id+"F12.wireOp",EDGE,"E49");var subQ2=makeQuery(id+"F12.imprint","INTERSECT",VERTEX,{"disambiguationData":[OD(0.0)],"derivedFrom":[subQ1,subQ0]});Q3=makeQuery(id+"F12.imprint","IMPRINT",FACE,{"disambiguationData":[TD([[makeQuery(id+"F12.imprint","IMPRINT",EDGE,{"disambiguationData":[TD([[subQ2,-1.0]])],"derivedFrom":subQ1}),1.0]])]});}
            var Q4;
            {var subQ0=sQuery(id+"F12.wireOp",EDGE,"E52");var subQ1=sQuery(id+"F12.wireOp",EDGE,"E49");var subQ2=makeQuery(id+"F12.imprint","INTERSECT",VERTEX,{"disambiguationData":[OD(0.0)],"derivedFrom":[subQ1,subQ0]});Q4=makeQuery(id+"F12.imprint","IMPRINT",FACE,{"disambiguationData":[TD([[makeQuery(id+"F12.imprint","IMPRINT",EDGE,{"disambiguationData":[TD([[subQ2,-1.0]])],"derivedFrom":subQ1}),1.0]])]});}
            var Q5;
            {var subQ0=sQuery(id+"F12.wireOp",EDGE,"E52");var subQ1=sQuery(id+"F12.wireOp",EDGE,"E49");var subQ2=makeQuery(id+"F12.imprint","INTERSECT",VERTEX,{"disambiguationData":[OD(0.0)],"derivedFrom":[subQ1,subQ0]});Q5=makeQuery(id+"F12.imprint","IMPRINT",FACE,{"disambiguationData":[TD([[makeQuery(id+"F12.imprint","IMPRINT",EDGE,{"disambiguationData":[TD([[subQ2,-1.0]])],"derivedFrom":subQ1}),-1.0]])]});}
            var Q6;
            {var subQ0=sQuery(id+"F12.wireOp",EDGE,"E53");var subQ1=sQuery(id+"F12.wireOp",EDGE,"E49");var subQ2=makeQuery(id+"F12.imprint","INTERSECT",VERTEX,{"disambiguationData":[OD(0.0)],"derivedFrom":[subQ1,subQ0]});Q6=makeQuery(id+"F12.imprint","IMPRINT",FACE,{"disambiguationData":[TD([[makeQuery(id+"F12.imprint","IMPRINT",EDGE,{"disambiguationData":[TD([[subQ2,1.0]])],"derivedFrom":subQ1}),1.0]])]});}
            var Q7;
            {var subQ0=sQuery(id+"F12.wireOp",EDGE,"E53");var subQ1=sQuery(id+"F12.wireOp",EDGE,"E49");var subQ2=makeQuery(id+"F12.imprint","INTERSECT",VERTEX,{"disambiguationData":[OD(0.0)],"derivedFrom":[subQ1,subQ0]});Q7=makeQuery(id+"F12.imprint","IMPRINT",FACE,{"disambiguationData":[TD([[makeQuery(id+"F12.imprint","IMPRINT",EDGE,{"disambiguationData":[TD([[subQ2,1.0]])],"derivedFrom":subQ1}),-1.0]])]});}
            extrude(context, id + "F13", {"entities" : qUnion([Q0, Q1, Q2, Q3, Q4, Q5, Q6, Q7]), "depth" : 228.6 * mm, "offsetDistance" : 25.4 * mm});
        }
        {
            var Q0;
            Q0=qCreatedBy(id+"F11.planeOp",FACE);
            var sketch = newSketch(context, id + "F14", { "sketchPlane" : qUnion([Q0])});
            skCircle(sketch, "E54", {"center": v(0, 0) * mm, "radius": 1511.3 * mm});
            skCircle(sketch, "E55", {"center": v(0, 0) * mm, "radius": 1600.2 * mm});
            skSolve(sketch);
        }
        {
            var Q0;
            Q0 = qSketchRegion(id + "F14", true);
            extrude(context, id + "F15", {"entities" : qUnion([Q0]), "depth" : 177.8 * mm, "offsetDistance" : 25.4 * mm, "hasSecondDirection" : true, "secondDirectionOppositeDirection" : false, "secondDirectionDepth" : 101.6 * mm});
        }
        {
            var Q0;
            Q0=makeQuery(id+"F13.opExtrude","CAP_FACE",FACE,{"disambiguationData":[OSD([sQuery(id+"F12.wireOp",EDGE,"E52")])],"isStart":false});
            var Q1;
            Q1=makeQuery(id+"F13.opExtrude","CAP_FACE",FACE,{"disambiguationData":[OSD([sQuery(id+"F12.wireOp",EDGE,"E53")])],"isStart":false});
            var Q2;
            Q2=makeQuery(id+"F13.opExtrude","CAP_FACE",FACE,{"disambiguationData":[OSD([sQuery(id+"F12.wireOp",EDGE,"E51")])],"isStart":false});
            var Q3;
            Q3=makeQuery(id+"F13.opExtrude","CAP_FACE",FACE,{"disambiguationData":[OSD([sQuery(id+"F12.wireOp",EDGE,"E50")])],"isStart":false});
            fillet(context, id + "F16", {"entities" : qUnion([Q0, Q1, Q2, Q3]), "radius" : 25.4 * mm, "tangentPropagation" : true, "allowEdgeOverflow" : false});
        }
        {
            var Q0;
            {var subQ2=sQuery(id+"F3.wireOp",EDGE,"E36");Q0=makeQuery(id+"F8.boolean.opBoolean","SPLIT",FACE,{"disambiguationData":[TD([makeQuery(id+"F8.opExtrude","SWEPT_FACE",FACE,{"disambiguationData":[OSD([sQuery(id+"F7.wireOp",EDGE,"E48.top")])]})])],"derivedFrom":makeQuery(id+"F6.opExtrude","SWEPT_FACE",FACE,{"disambiguationData":[OSD([subQ2])]})});}
            var sketch = newSketch(context, id + "F17", { "sketchPlane" : qUnion([Q0])});
            skLineSegment(sketch, "E56", {"start": v(-370.8, 1736.96) * mm, "end": v(-142.85, 1736.96) * mm});
            skLineSegment(sketch, "E57", {"start": v(-142.85, 1660.44) * mm, "end": v(-142.85, 1736.96) * mm});
            skLineSegment(sketch, "E58", {"start": v(-142.85, 1660.44) * mm, "end": v(-72.84, 1660.44) * mm});
            skLineSegment(sketch, "E59", {"start": v(-72.84, 1579.03) * mm, "end": v(-72.84, 1660.44) * mm});
            skLineSegment(sketch, "E60", {"start": v(-72.84, 1579.03) * mm, "end": v(19.97, 1579.03) * mm});
            skLineSegment(sketch, "E61", {"start": v(19.97, 1699.51) * mm, "end": v(19.97, 1579.03) * mm});
            skLineSegment(sketch, "E62", {"start": v(19.97, 1699.51) * mm, "end": v(130.69, 1699.51) * mm});
            skLineSegment(sketch, "E63", {"start": v(130.69, 1629.5) * mm, "end": v(130.69, 1699.51) * mm});
            skLineSegment(sketch, "E64", {"start": v(130.69, 1629.5) * mm, "end": v(322.82, 1629.5) * mm});
            skLineSegment(sketch, "E65", {"start": v(322.82, 1321.77) * mm, "end": v(322.82, 1629.5) * mm});
            skLineSegment(sketch, "E66", {"start": v(322.82, 1321.77) * mm, "end": v(186.05, 1321.77) * mm});
            skLineSegment(sketch, "E67", {"start": v(186.05, 1321.77) * mm, "end": v(186.05, 1439) * mm});
            skLineSegment(sketch, "E68", {"start": v(186.05, 1439) * mm, "end": v(186.05, 1497.62) * mm});
            skLineSegment(sketch, "E69", {"start": v(-185.18, 1321.77) * mm, "end": v(-305.67, 1321.77) * mm});
            skLineSegment(sketch, "E70", {"start": v(-305.67, 1321.77) * mm, "end": v(-370.8, 1736.96) * mm});
            skLineSegment(sketch, "E71", {"start": v(186.05, 1497.62) * mm, "end": v(130.56, 1497.62) * mm});
            skLineSegment(sketch, "E72", {"start": v(130.56, 1497.62) * mm, "end": v(130.56, 1372.74) * mm});
            skLineSegment(sketch, "E73", {"start": v(0, 1372.74) * mm, "end": v(130.56, 1372.74) * mm});
            skLineSegment(sketch, "E74", {"start": v(0, 1413.77) * mm, "end": v(0, 1372.74) * mm});
            skLineSegment(sketch, "E75", {"start": v(0, 1413.77) * mm, "end": v(-137.76, 1413.77) * mm});
            skLineSegment(sketch, "E76", {"start": v(-137.76, 1413.77) * mm, "end": v(-137.76, 1321.66) * mm});
            skLineSegment(sketch, "E77", {"start": v(-185.18, 1321.77) * mm, "end": v(-153.35, 1321.77) * mm});
            skLineSegment(sketch, "E78", {"start": v(-153.35, 1321.77) * mm, "end": v(-137.76, 1321.77) * mm});
            skSolve(sketch);
        }
        {
            var Q0;
            Q0 = qSketchRegion(id + "F17", true);
            extrude(context, id + "F18", {"entities" : qUnion([Q0]), "operationType" : NewBodyOperationType.REMOVE, "oppositeDirection" : true, "depth" : 459.74 * mm, "offsetDistance" : 25.4 * mm});
        }
        {
            var Q0;
            Q0=qCreatedBy(id+"F11.planeOp",FACE);
            var sketch = newSketch(context, id + "F19", { "sketchPlane" : qUnion([Q0])});
            skLineSegment(sketch, "E79", {"start": v(1303.22, -605.6) * mm, "end": v(1057.8, -972.95) * mm});
            skLineSegment(sketch, "E80", {"start": v(1057.8, -972.95) * mm, "end": v(1283.96, -1124.04) * mm});
            skLineSegment(sketch, "E81", {"start": v(1283.96, -1124.04) * mm, "end": v(1529.66, -756.26) * mm});
            skLineSegment(sketch, "E82", {"start": v(1529.66, -756.26) * mm, "end": v(1303.22, -605.6) * mm});
            skSolve(sketch);
        }
        {
            var Q0;
            Q0 = qSketchRegion(id + "F19", true);
            extrude(context, id + "F20", {"entities" : qUnion([Q0]), "operationType" : NewBodyOperationType.REMOVE, "oppositeDirection" : true, "depth" : 2268.22 * mm, "offsetDistance" : 25.4 * mm, "hasSecondDirection" : true, "secondDirectionOppositeDirection" : true, "secondDirectionDepth" : 50.8 * mm});
        }
        {
            var Q0;
            Q0=qCreatedBy(id+"F11.planeOp",FACE);
            var sketch = newSketch(context, id + "F21", { "sketchPlane" : qUnion([Q0])});
            skCircle(sketch, "E83", {"center": v(0, 0) * mm, "radius": 1778 * mm});
            skCircle(sketch, "E84", {"center": v(0, 0) * mm, "radius": 1771.65 * mm});
            skLineSegment(sketch, "E85", {"start": v(0, 0) * mm, "end": v(-1778.93, 1775.89) * mm});
            skLineSegment(sketch, "E86", {"start": v(0, 0) * mm, "end": v(1772.85, 1775.89) * mm});
            skSolve(sketch);
        }
        {
            var Q0;
            {var subQ0=sQuery(id+"F21.wireOp",EDGE,"E85");var subQ1=sQuery(id+"F21.wireOp",EDGE,"E83");var subQ2=makeQuery(id+"F21.imprint","INTERSECT",VERTEX,{"derivedFrom":[subQ1,subQ0]});Q0=makeQuery(id+"F21.imprint","IMPRINT",FACE,{"disambiguationData":[TD([[makeQuery(id+"F21.imprint","IMPRINT",EDGE,{"disambiguationData":[TD([[subQ2,1.0]])],"derivedFrom":subQ1}),1.0]])]});}
            extrude(context, id + "F22", {"entities" : qUnion([Q0]), "oppositeDirection" : true, "depth" : 1219.2 * mm, "offsetDistance" : 25.4 * mm});
        }
    });
